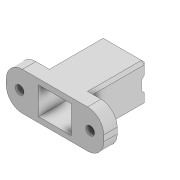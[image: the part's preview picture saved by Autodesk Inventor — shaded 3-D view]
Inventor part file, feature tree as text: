
AUTODESK INVENTOR PART (.ipt)
format: ipt  version: 2022 (Build 260153000, 153)  size: 226,304 bytes
history: native  units: mm
features: projected_geometry x6, extrude x5, sketch x5, other x1, shell x1, fillet x1, chamfer x1
ambient origin geometry x8: Origin, YZ Plane, XZ Plane, XY Plane, X Axis, Y Axis, Z Axis, Center Point
bodies: Body1 (feature_tree)
feature tree (20):
  other  "Sólido1"
  extrude  "Extrusión1"  Depth=10.2mm
  shell  "Vaciado1"  Thickness=2.0mm
  extrude  "Extrusión2"  Depth=2.0mm
  extrude  "Extrusión3"  Depth=5.5mm
  extrude  "Extrusión4"  Depth=5.0mm TaperAngle=0.0deg
  extrude  "Extrusión5"  Depth=10.0mm
  fillet  "Empalme1"  Radius=10.0mm
  chamfer  "Chaflán1"  Distance=6.0mm
  sketch  "Boceto1"  dims[d0=12.2mm d1=10.2mm d2=2.0mm]
  sketch  "Boceto2"  dims[d3=26.0mm d4=0.0mm d5=2.0mm]
  projected_geometry  "Contorno proyectado1"
  sketch  "Boceto3"  dims[d6=5.5mm d7=2.75mm]
  projected_geometry  "Contorno proyectado2"
  sketch  "Boceto4"  dims[d8=2.0mm d9=0.0mm d16=5.0mm d17=0.0mm]
  projected_geometry  "Contorno proyectado3"
  projected_geometry  "Contorno proyectado4"
  sketch  "Boceto5"  dims[d18=14.2mm d19=10.0mm d20=10.0mm d21=6.0mm d22=3.0mm d23=7.0mm d24=3.5mm d25=4.0mm d26=4.0mm d27=2.0mm d28=2.0mm d29=2.5mm d30=0.0mm d31=3.2mm d32=3.2mm d33=0.0mm d34=0.0mm d35=6.0mm d36=1.0mm d37=2.0mm d38=45.0deg]
  projected_geometry  "Contorno proyectado5"
  projected_geometry  "Contorno proyectado6"
